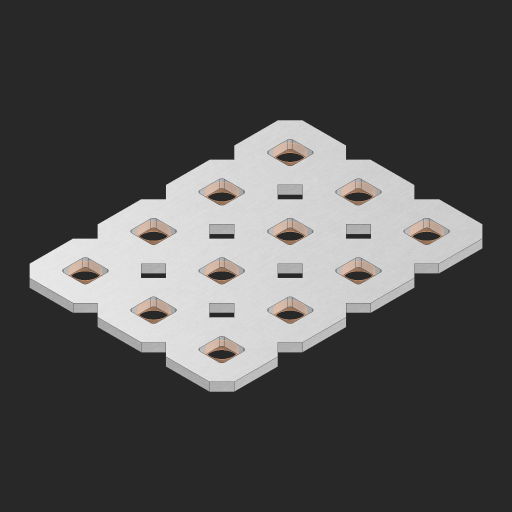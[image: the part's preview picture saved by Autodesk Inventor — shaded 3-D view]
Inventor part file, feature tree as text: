
AUTODESK INVENTOR PART (.ipt)
format: ipt  version: 2023 (Build 270158000, 158)  size: 435,712 bytes
history: native  units: in
note: dims shown in document units (in); Inventor stores cm internally (conversion verified against a paired STEP export)
features: other x13, extrude x11, sketch x2, pattern_linear x1
ambient origin geometry x8: Origin, YZ Plane, XZ Plane, XY Plane, X Axis, Y Axis, Z Axis, Center Point
bodies: Solid1 (feature_tree), Body (feature_tree)
feature tree (27):
  pattern_linear  "Rectangular Pattern1"  Spacing1=0.09in  [1 undecoded]
  sketch  "Sketch1"  dims[d1=0.5in]
  sketch  "Sketch2"  dims[d2=0.182in d3=0.09in d4=0.09in d5=0.09in d6=0.09in d7=0.09in d8=0.09in d9=0.09in d10=0.09in d11=0.02in d13=0.0in d14=0.172in d15=0.0625in d16=0.0in d19=0.5in d22=0.5in]
  other  "Srf1"
  other  "Srf126"
  other  "Srf127"
  other  "Srf128"
  other  "Srf268"
  other  "Srf269"
  other  "Srf270"
  other  "Srf271"
  other  "Srf293"
  other  "Srf294"
  other  "Srf295"
  other  "Srf296"
  other  "Circle"
  extrude  "ExtrusionSrf126"  Depth=0.09in
  extrude  "ExtrusionSrf127"  Depth=0.09in
  extrude  "ExtrusionSrf128"  Depth=0.09in
  extrude  "ExtrusionSrf268"  Depth=0.09in
  extrude  "ExtrusionSrf269"  Depth=0.09in
  extrude  "ExtrusionSrf270"  Depth=0.09in
  extrude  "ExtrusionSrf271"  Depth=0.09in
  extrude  "ExtrusionSrf293"  Depth=0.02in
  extrude  "ExtrusionSrf294"  TaperAngle=0.0deg  [1 undecoded]
  extrude  "ExtrusionSrf295"  Depth=0.5in
  extrude  "ExtrusionSrf296"  Depth=0.0625in TaperAngle=0.0deg
note: 2 required parameter values undecoded (feature->parameter linkage not recoverable at this tier; creation-order binding heuristic only, values carry confidence <= 0.55)
